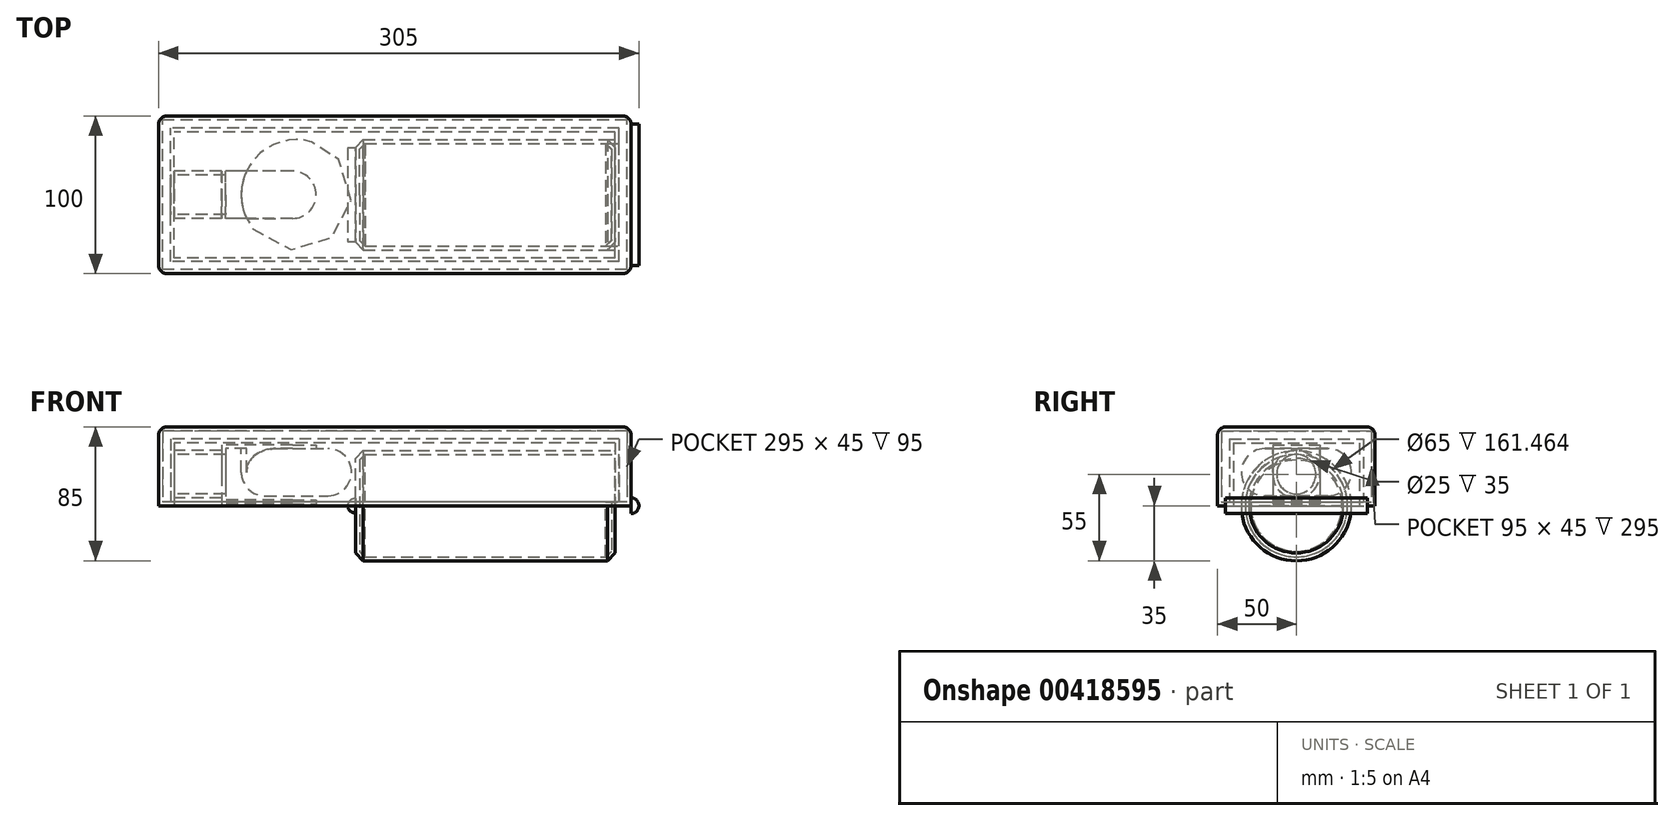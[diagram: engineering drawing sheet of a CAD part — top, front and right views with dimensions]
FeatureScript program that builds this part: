
annotation { "Feature Type Name" : "Feature", "Feature Type Description" : "" }
export const myFeature = defineFeature(function(context is Context, id is Id, definition is map)
    precondition{}
    {
        {
            var Q0;
            Q0=qCreatedBy(makeId("Top.planeOp"),FACE);
            var sketch = newSketch(context, id + "F0", { "sketchPlane" : qUnion([Q0])});
            skLineSegment(sketch, "E0.bottom", {"start": v(150, -50) * mm, "end": v(-150, -50) * mm});
            skLineSegment(sketch, "E0.top", {"start": v(150, 50) * mm, "end": v(-150, 50) * mm});
            skLineSegment(sketch, "E0.left", {"start": v(150, -50) * mm, "end": v(150, 50) * mm});
            skLineSegment(sketch, "E0.right", {"start": v(-150, -50) * mm, "end": v(-150, 50) * mm});
            skPoint(sketch, "E0.middle", {"position": v(0, 0) * mm});
            skSolve(sketch);
        }
        {
            var Q0;
            Q0=makeQuery(id+"F0.imprint","IMPRINT",FACE,{"disambiguationData":[TD([[makeQuery(id+"F0.imprint","IMPRINT",EDGE,{"derivedFrom":sQuery(id+"F0.wireOp",EDGE,"E0.bottom")}),-1.0]])]});
            extrude(context, id + "F1", {"entities" : qUnion([Q0]), "depth" : 50 * mm});
        }
        {
            var Q0;
            Q0=makeQuery(id+"F1.opExtrude","CAP_FACE",FACE,{"disambiguationData":[OSD([sQuery(id+"F0.wireOp",EDGE,"E0.bottom"),sQuery(id+"F0.wireOp",EDGE,"E0.top"),sQuery(id+"F0.wireOp",EDGE,"E0.left"),sQuery(id+"F0.wireOp",EDGE,"E0.right")])],"isStart":true});
            shell(context, id + "F2", {"entities" : qUnion([Q0]), "thickness" : 10 * mm});
        }
        {
            var Q0;
            Q0=makeQuery(id+"F2.opShell","OFFSET_FACE",FACE,{"disambiguationData":[OSD([sQuery(id+"F0.wireOp",EDGE,"E0.left")])]});
            var sketch = newSketch(context, id + "F3", { "sketchPlane" : qUnion([Q0])});
            skCircle(sketch, "E1", {"center": v(0, 0) * mm, "radius": 35 * mm});
            skSolve(sketch);
        }
        {
            var Q0;
            Q0 = qSketchRegion(id + "F3", true);
            extrude(context, id + "F4", {"entities" : qUnion([Q0]), "operationType" : NewBodyOperationType.ADD, "depth" : 165 * mm});
        }
        {
            var Q0;
            {var subQ0=sQuery(id+"F3.wireOp",EDGE,"E1");Q0=makeQuery(id+"F4.boolean.opBoolean","SPLIT",EDGE,{"disambiguationData":[topologyDisambiguationEdgeConnected([makeQuery(id+"F4.opExtrude","CAP_FACE",FACE,{"disambiguationData":[OSD([subQ0])],"isStart":true})])],"derivedFrom":makeQuery(id+"F4.opExtrude","CAP_EDGE",EDGE,{"disambiguationData":[OSD([subQ0])],"isStart":true})});}
            var Q1;
            Q1=makeQuery(id+"F4.opExtrude","CAP_EDGE",EDGE,{"disambiguationData":[OSD([sQuery(id+"F3.wireOp",EDGE,"E1")])],"isStart":false});
            chamfer(context, id + "F5", {"entities" : qUnion([Q0, Q1]), "width" : 5 * mm, "tangentPropagation" : true});
        }
        {
            var Q0;
            Q0=makeQuery(id+"F2.opShell","OFFSET_FACE",FACE,{"disambiguationData":[OSD([sQuery(id+"F0.wireOp",EDGE,"E0.right")])]});
            var sketch = newSketch(context, id + "F6", { "sketchPlane" : qUnion([Q0])});
            skLineSegment(sketch, "E2", {"start": v(0, 0) * mm, "end": v(0, 20) * mm});
            skPoint(sketch, "E2.endSnap0", {"position": v(0, 0) * mm});
            skCircle(sketch, "E3", {"center": v(0, 20) * mm, "radius": 15 * mm});
            skSolve(sketch);
        }
        {
            var Q0;
            Q0 = qSketchRegion(id + "F6", true);
            extrude(context, id + "F7", {"entities" : qUnion([Q0]), "operationType" : NewBodyOperationType.ADD, "depth" : 30 * mm});
        }
        {
            var Q0;
            Q0=makeQuery(id+"F7.opExtrude","CAP_FACE",FACE,{"disambiguationData":[OSD([sQuery(id+"F6.wireOp",EDGE,"E3")])],"isStart":false});
            var sketch = newSketch(context, id + "F8", { "sketchPlane" : qUnion([Q0])});
            skLineSegment(sketch, "E4.bottom", {"start": v(-15, 38.75) * mm, "end": v(15, 38.75) * mm});
            skLineSegment(sketch, "E4.top", {"start": v(-15, 1.25) * mm, "end": v(15, 1.25) * mm});
            skLineSegment(sketch, "E4.left", {"start": v(-15, 38.75) * mm, "end": v(-15, 1.25) * mm});
            skLineSegment(sketch, "E4.right", {"start": v(15, 38.75) * mm, "end": v(15, 1.25) * mm});
            skPoint(sketch, "E4.middle", {"position": v(0, 20) * mm});
            skSolve(sketch);
        }
        {
            var Q0;
            Q0 = qSketchRegion(id + "F8", true);
            extrude(context, id + "F9", {"entities" : qUnion([Q0]), "operationType" : NewBodyOperationType.ADD, "depth" : 60 * mm});
        }
        {
            var Q0;
            Q0=makeQuery(id+"F9.opExtrude","SWEPT_FACE",FACE,{"disambiguationData":[OSD([sQuery(id+"F8.wireOp",EDGE,"E4.left")])]});
            var Q1;
            Q1=makeQuery(id+"F9.opExtrude","SWEPT_FACE",FACE,{"disambiguationData":[OSD([sQuery(id+"F8.wireOp",EDGE,"E4.right")])]});
            var Q2;
            Q2=makeQuery(id+"F9.opExtrude","CAP_FACE",FACE,{"disambiguationData":[OSD([sQuery(id+"F8.wireOp",EDGE,"E4.bottom"),sQuery(id+"F8.wireOp",EDGE,"E4.top"),sQuery(id+"F8.wireOp",EDGE,"E4.left"),sQuery(id+"F8.wireOp",EDGE,"E4.right")])],"isStart":false});
            shell(context, id + "F10", {"entities" : qUnion([Q0, Q1, Q2]), "thickness" : 2.5 * mm});
        }
        {
            var Q0;
            Q0=makeQuery(id+"F10.opShell","OFFSET_FACE",FACE,{"disambiguationData":[OSD([sQuery(id+"F8.wireOp",EDGE,"E4.bottom")])]});
            var sketch = newSketch(context, id + "F11", { "sketchPlane" : qUnion([Q0])});
            skLineSegment(sketch, "E5", {"start": v(-107.5, 0) * mm, "end": v(-62.5, 0) * mm});
            skCircle(sketch, "E6", {"center": v(-62.5, 0) * mm, "radius": 35 * mm});
            skSolve(sketch);
        }
        {
            var Q0;
            {var subQ1=sQuery(id+"F8.wireOp",EDGE,"E4.bottom");var subQ6=makeQuery(id+"F10.opShell","OFFSET_EDGE",EDGE,{"disambiguationData":[OSD([subQ1]),TDD([makeQuery(id+"F9.opExtrude","CAP_EDGE",EDGE,{"disambiguationData":[OSD([subQ1])],"isStart":false})])]});Q0=makeQuery(id+"F11.imprint","IMPRINT",FACE,{"disambiguationData":[TD([[makeQuery(id+"F11.imprint","IMPRINT",EDGE,{"derivedFrom":subQ6}),1.0]])]});}
            var Q1;
            {var subQ0=sQuery(id+"F8.wireOp",EDGE,"E4.bottom");var subQ1=makeQuery(id+"F10.opShell","OFFSET_EDGE",EDGE,{"disambiguationData":[OSD([subQ0]),TDD([makeQuery(id+"F9.opExtrude","CAP_EDGE",EDGE,{"disambiguationData":[OSD([subQ0])],"isStart":false})])]});Q1=makeQuery(id+"F11.imprint","IMPRINT",FACE,{"disambiguationData":[TD([[makeQuery(id+"F11.imprint","IMPRINT",EDGE,{"derivedFrom":subQ1}),-1.0]])]});}
            extrude(context, id + "F12", {"entities" : qUnion([Q0, Q1]), "operationType" : NewBodyOperationType.ADD, "depth" : 30 * mm});
        }
        {
            var Q0;
            {var subQ0=sQuery(id+"F11.wireOp",EDGE,"E6");Q0=makeQuery(id+"F12.boolean.opBoolean","SPLIT",EDGE,{"disambiguationData":[topologyDisambiguationEdgeConnected([makeQuery(id+"F12.opExtrude","CAP_FACE",FACE,{"disambiguationData":[OSD([subQ0])],"isStart":true})])],"derivedFrom":makeQuery(id+"F12.opExtrude","CAP_EDGE",EDGE,{"disambiguationData":[OSD([subQ0])],"isStart":true})});}
            var Q1;
            Q1=makeQuery(id+"F12.opExtrude","CAP_EDGE",EDGE,{"disambiguationData":[OSD([sQuery(id+"F11.wireOp",EDGE,"E6")])],"isStart":false});
            fillet(context, id + "F13", {"entities" : qUnion([Q0, Q1]), "radius" : 15 * mm, "tangentPropagation" : true, "allowEdgeOverflow" : false});
        }
        {
            var Q0;
            {var subQ0=sQuery(id+"F8.wireOp",EDGE,"E4.right");Q0=makeQuery(id+"F10.opShell","OFFSET_EDGE",EDGE,{"disambiguationData":[OSD([subQ0]),TDD([makeQuery(id+"F9.opExtrude","CAP_EDGE",EDGE,{"disambiguationData":[OSD([subQ0])],"isStart":false})])]});}
            var Q1;
            {var subQ0=sQuery(id+"F8.wireOp",EDGE,"E4.left");Q1=makeQuery(id+"F10.opShell","OFFSET_EDGE",EDGE,{"disambiguationData":[OSD([subQ0]),TDD([makeQuery(id+"F9.opExtrude","CAP_EDGE",EDGE,{"disambiguationData":[OSD([subQ0])],"isStart":false})])]});}
            fillet(context, id + "F14", {"entities" : qUnion([Q0, Q1]), "radius" : 15 * mm, "tangentPropagation" : true, "allowEdgeOverflow" : false});
        }
        {
            var Q0;
            Q0=makeQuery(id+"F1.opExtrude","CAP_EDGE",EDGE,{"disambiguationData":[OSD([sQuery(id+"F0.wireOp",EDGE,"E0.top")])],"isStart":false});
            var Q1;
            Q1=makeQuery(id+"F1.opExtrude","CAP_EDGE",EDGE,{"disambiguationData":[OSD([sQuery(id+"F0.wireOp",EDGE,"E0.bottom")])],"isStart":false});
            var Q2;
            Q2=makeQuery(id+"F1.opExtrude","SWEPT_EDGE",EDGE,{"disambiguationData":[OSD([sQuery(id+"F0.wireOp",EDGE,"E0.bottom"),sQuery(id+"F0.wireOp",EDGE,"E0.left")])]});
            var Q3;
            Q3=makeQuery(id+"F1.opExtrude","CAP_EDGE",EDGE,{"disambiguationData":[OSD([sQuery(id+"F0.wireOp",EDGE,"E0.left")])],"isStart":false});
            var Q4;
            Q4=makeQuery(id+"F1.opExtrude","SWEPT_EDGE",EDGE,{"disambiguationData":[OSD([sQuery(id+"F0.wireOp",EDGE,"E0.top"),sQuery(id+"F0.wireOp",EDGE,"E0.left")])]});
            var Q5;
            Q5=makeQuery(id+"F1.opExtrude","SWEPT_EDGE",EDGE,{"disambiguationData":[OSD([sQuery(id+"F0.wireOp",EDGE,"E0.top"),sQuery(id+"F0.wireOp",EDGE,"E0.right")])]});
            var Q6;
            Q6=makeQuery(id+"F1.opExtrude","SWEPT_EDGE",EDGE,{"disambiguationData":[OSD([sQuery(id+"F0.wireOp",EDGE,"E0.bottom"),sQuery(id+"F0.wireOp",EDGE,"E0.right")])]});
            var Q7;
            Q7=makeQuery(id+"F1.opExtrude","CAP_EDGE",EDGE,{"disambiguationData":[OSD([sQuery(id+"F0.wireOp",EDGE,"E0.right")])],"isStart":false});
            fillet(context, id + "F15", {"entities" : qUnion([Q0, Q1, Q2, Q3, Q4, Q5, Q6, Q7]), "radius" : 5 * mm, "tangentPropagation" : true, "allowEdgeOverflow" : false});
        }
        {
            var Q0;
            Q0=makeQuery(id+"F4.opExtrude","CAP_FACE",FACE,{"disambiguationData":[OSD([sQuery(id+"F3.wireOp",EDGE,"E1")])],"isStart":false});
            var sketch = newSketch(context, id + "F16", { "sketchPlane" : qUnion([Q0])});
            skLineSegment(sketch, "E7.bottom", {"start": v(-29.64, -4.63) * mm, "end": v(29.64, -4.63) * mm});
            skLineSegment(sketch, "E7.top", {"start": v(-29.64, 4.63) * mm, "end": v(29.64, 4.63) * mm});
            skLineSegment(sketch, "E7.left", {"start": v(-29.64, -4.63) * mm, "end": v(-29.64, 4.63) * mm});
            skLineSegment(sketch, "E7.right", {"start": v(29.64, -4.63) * mm, "end": v(29.64, 4.63) * mm});
            skPoint(sketch, "E7.middle", {"position": v(0, 0) * mm});
            skSolve(sketch);
        }
        {
            var Q0;
            Q0 = qSketchRegion(id + "F16", true);
            extrude(context, id + "F17", {"entities" : qUnion([Q0]), "operationType" : NewBodyOperationType.ADD, "depth" : 5 * mm});
        }
        {
            var Q0;
            Q0=makeQuery(id+"F17.opExtrude","CAP_EDGE",EDGE,{"disambiguationData":[OSD([sQuery(id+"F16.wireOp",EDGE,"E7.top")])],"isStart":false});
            var Q1;
            Q1=makeQuery(id+"F17.opExtrude","CAP_EDGE",EDGE,{"disambiguationData":[OSD([sQuery(id+"F16.wireOp",EDGE,"E7.bottom")])],"isStart":false});
            fillet(context, id + "F18", {"entities" : qUnion([Q0, Q1]), "radius" : 5 * mm, "tangentPropagation" : true, "allowEdgeOverflow" : false});
        }
        {
            var Q0;
            Q0=makeQuery(id+"F1.opExtrude","SWEPT_FACE",FACE,{"disambiguationData":[OSD([sQuery(id+"F0.wireOp",EDGE,"E0.left")])]});
            var sketch = newSketch(context, id + "F19", { "sketchPlane" : qUnion([Q0])});
            skLineSegment(sketch, "E8.bottom", {"start": v(-45, -5) * mm, "end": v(45, -5) * mm});
            skLineSegment(sketch, "E8.top", {"start": v(-45, 5) * mm, "end": v(45, 5) * mm});
            skLineSegment(sketch, "E8.left", {"start": v(-45, -5) * mm, "end": v(-45, 5) * mm});
            skLineSegment(sketch, "E8.right", {"start": v(45, -5) * mm, "end": v(45, 5) * mm});
            skPoint(sketch, "E8.middle", {"position": v(0, 0) * mm});
            skSolve(sketch);
        }
        {
            var Q0;
            Q0 = qSketchRegion(id + "F19", true);
            extrude(context, id + "F20", {"entities" : qUnion([Q0]), "operationType" : NewBodyOperationType.ADD, "depth" : 5 * mm});
        }
        {
            var Q0;
            Q0=makeQuery(id+"F20.opExtrude","CAP_EDGE",EDGE,{"disambiguationData":[OSD([sQuery(id+"F19.wireOp",EDGE,"E8.top")])],"isStart":false});
            var Q1;
            Q1=makeQuery(id+"F20.opExtrude","CAP_EDGE",EDGE,{"disambiguationData":[OSD([sQuery(id+"F19.wireOp",EDGE,"E8.bottom")])],"isStart":false});
            fillet(context, id + "F21", {"entities" : qUnion([Q0, Q1]), "radius" : 5 * mm, "tangentPropagation" : true, "allowEdgeOverflow" : false});
        }
        {
            var Q0;
            Q0=makeQuery(id+"F9.opExtrude","CAP_EDGE",EDGE,{"disambiguationData":[OSD([sQuery(id+"F8.wireOp",EDGE,"E4.right")])],"isStart":false});
            var Q1;
            Q1=makeQuery(id+"F9.opExtrude","CAP_EDGE",EDGE,{"disambiguationData":[OSD([sQuery(id+"F8.wireOp",EDGE,"E4.left")])],"isStart":false});
            fillet(context, id + "F22", {"entities" : qUnion([Q0, Q1]), "radius" : 15 * mm, "tangentPropagation" : true, "allowEdgeOverflow" : false});
        }
    });
